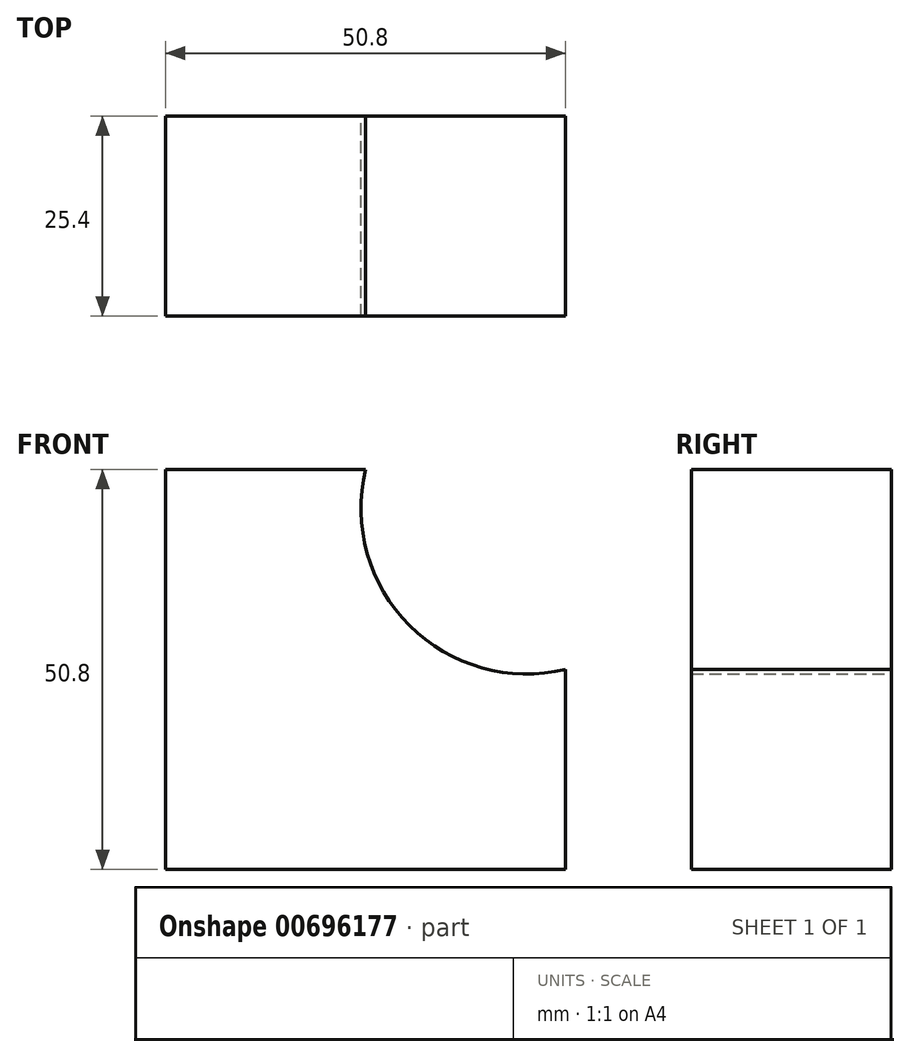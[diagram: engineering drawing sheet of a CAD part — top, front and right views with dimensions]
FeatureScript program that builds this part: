
annotation { "Feature Type Name" : "Feature", "Feature Type Description" : "" }
export const myFeature = defineFeature(function(context is Context, id is Id, definition is map)
    precondition{}
    {
        {
            var Q0;
            Q0=qCreatedBy(makeId("Front.planeOp"),FACE);
            var sketch = newSketch(context, id + "F0", { "sketchPlane" : qUnion([Q0])});
            skLineSegment(sketch, "E0", {"start": v(-47.07, 42.88) * mm, "end": v(-47.07, -7.92) * mm});
            skLineSegment(sketch, "E1", {"start": v(-47.07, -7.92) * mm, "end": v(3.73, -7.92) * mm});
            skLineSegment(sketch, "E2", {"start": v(-47.07, 42.88) * mm, "end": v(-21.67, 42.88) * mm});
            skLineSegment(sketch, "E3", {"start": v(3.73, -7.92) * mm, "end": v(3.73, 17.48) * mm});
            skArc(sketch, "E4", {"start": v(-21.67, 42.88) * mm, "mid": v(-16.08, 23.07) * mm, "end": v(3.73, 17.48) * mm});
            skSolve(sketch);
        }
        {
            var Q0;
            Q0 = qSketchRegion(id + "F0", true);
            extrude(context, id + "F1", {"entities" : qUnion([Q0]), "depth" : 25.4 * mm, "offsetDistance" : 25.4 * mm});
        }
    });
